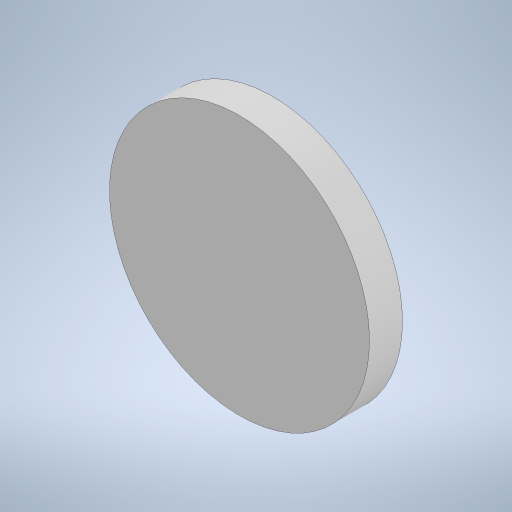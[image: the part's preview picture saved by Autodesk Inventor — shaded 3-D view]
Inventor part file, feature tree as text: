
AUTODESK INVENTOR PART (.ipt)
format: ipt  version: 2024 (Build 280153000, 153)  size: 208,384 bytes
history: native  units: in
note: dims shown in document units (in); Inventor stores cm internally (conversion verified against a paired STEP export)
features: extrude x1, sketch x1
ambient origin geometry x8: Origin, YZ Plane, XZ Plane, XY Plane, X Axis, Y Axis, Z Axis, Center Point
bodies: Solid1 (feature_tree)
feature tree (2):
  extrude  "Extrusion1"  Depth=5.0in TaperAngle=0.0deg
  sketch  "Sketch1"  dims[d0=39.3701in d1=5.0in d2=0.0in]
